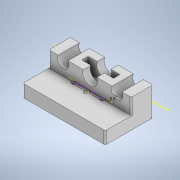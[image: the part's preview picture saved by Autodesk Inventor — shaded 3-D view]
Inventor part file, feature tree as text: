
AUTODESK INVENTOR PART (.ipt)
format: ipt  version: 2021 (Build 250183000, 183)  size: 371,200 bytes
history: native  units: in
note: dims shown in document units (in); Inventor stores cm internally (conversion verified against a paired STEP export)
features: sketch x6, extrude x5, projected_geometry x5, fillet x3
ambient origin geometry x8: Origin, YZ Plane, XZ Plane, XY Plane, X Axis, Y Axis, Z Axis, Center Point
bodies: Solid1 (feature_tree)
feature tree (19):
  extrude  "Extrusion1"  Depth=0.7874in
  extrude  "Extrusion2"  Depth=0.5906in
  sketch  "Sketch4"  dims[d5=0.3248in d6=1.4921in]
  sketch  "Sketch5"  dims[d7=0.0886in d8=0.0in d9=0.0in]
  extrude  "Extrusion3"  Depth=1.4921in
  extrude  "Extrusion4"  TaperAngle=0.0deg  [1 undecoded]
  extrude  "Extrusion5"  Depth=0.3937in
  fillet  "Fillet4"  Radius=0.8819in
  fillet  "Fillet5"  Radius=0.1772in
  fillet  "Fillet6"  Radius=0.3937in
  sketch  "Sketch1"  dims[d0=2.2835in d1=0.7874in]
  sketch  "Sketch3"  dims[d2=0.5906in d3=0.0in d4=0.3248in]
  projected_geometry  "Projected Loop2"
  projected_geometry  "Projected Loop3"
  projected_geometry  "Projected Loop4"
  sketch  "Sketch6"  dims[d10=0.8858in d11=0.2165in d12=0.8819in d13=0.1772in d14=0.3937in d15=0.0in]
  projected_geometry  "Projected Loop5"
  sketch  "Sketch8"  dims[d16=0.4134in d17=0.0in d18=0.0in d19=0.3543in d20=0.7205in d21=0.0in d25=0.0394in d26=0.0394in d27=0.0197in]
  projected_geometry  "Projected Loop7"
note: 1 required parameter value undecoded (feature->parameter linkage not recoverable at this tier; creation-order binding heuristic only, values carry confidence <= 0.55)
